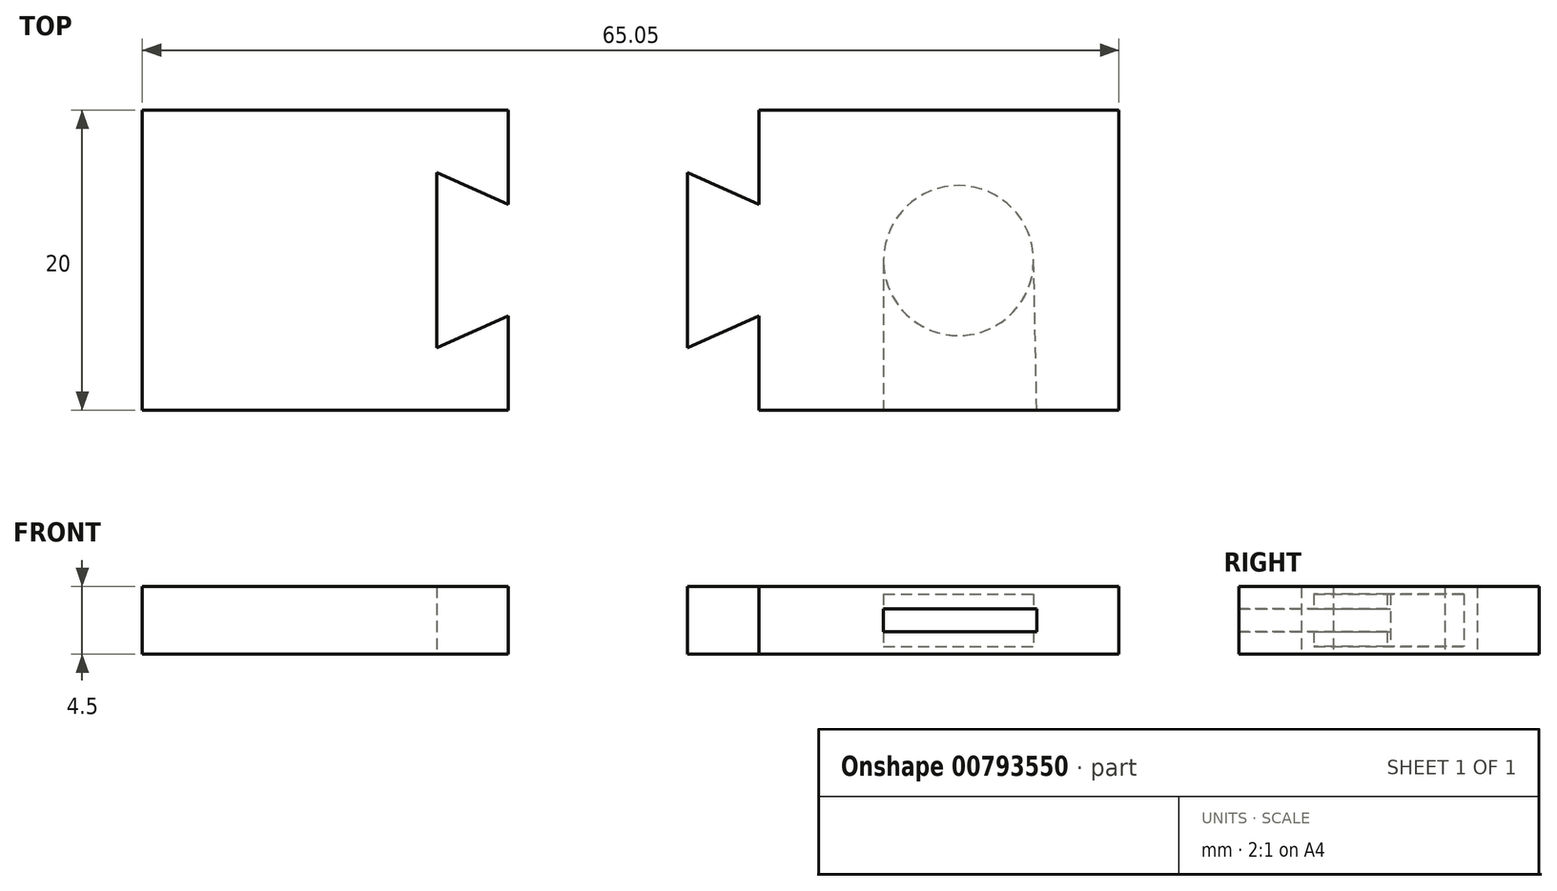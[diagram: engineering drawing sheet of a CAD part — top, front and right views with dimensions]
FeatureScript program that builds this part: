
annotation { "Feature Type Name" : "Feature", "Feature Type Description" : "" }
export const myFeature = defineFeature(function(context is Context, id is Id, definition is map)
    precondition{}
    {
        {
            var Q0;
            Q0=qCreatedBy(makeId("Top.planeOp"),FACE);
            var sketch = newSketch(context, id + "F0", { "sketchPlane" : qUnion([Q0])});
            skLineSegment(sketch, "E0.bottom", {"start": v(-24.37, 20) * mm, "end": v(23.98, 20) * mm});
            skLineSegment(sketch, "E0.top", {"start": v(-24.37, 0) * mm, "end": v(23.98, 0) * mm});
            skLineSegment(sketch, "E0.left", {"start": v(-24.37, 20) * mm, "end": v(-24.37, 0) * mm});
            skLineSegment(sketch, "E0.right", {"start": v(23.98, 20) * mm, "end": v(23.98, 0) * mm});
            skLineSegment(sketch, "E1", {"start": v(0, 20) * mm, "end": v(0, 13.72) * mm});
            skLineSegment(sketch, "E2", {"start": v(0, 13.72) * mm, "end": v(-4.78, 15.86) * mm});
            skLineSegment(sketch, "E3", {"start": v(-4.78, 15.86) * mm, "end": v(-4.78, 4.14) * mm});
            skLineSegment(sketch, "E4", {"start": v(-4.78, 4.14) * mm, "end": v(0, 6.28) * mm});
            skLineSegment(sketch, "E5", {"start": v(0, 6.28) * mm, "end": v(0, 0) * mm});
            skSolve(sketch);
        }
        {
            var Q0;
            {var subQ1=sQuery(id+"F0.wireOp",EDGE,"E0.left");Q0=makeQuery(id+"F0.imprint","IMPRINT",FACE,{"disambiguationData":[TD([[makeQuery(id+"F0.imprint","IMPRINT",EDGE,{"derivedFrom":subQ1}),1.0]])]});}
            extrude(context, id + "F1", {"entities" : qUnion([Q0]), "depth" : 4.5 * mm, "offsetDistance" : 25 * mm});
        }
        {
            var Q0;
            Q0=makeQuery(id+"F1.opExtrude","SWEPT_BODY",BODY,{"disambiguationData":[OSD([sQuery(id+"F0.wireOp",EDGE,"E0.bottom"),sQuery(id+"F0.wireOp",EDGE,"E0.top"),sQuery(id+"F0.wireOp",EDGE,"E0.left"),sQuery(id+"F0.wireOp",EDGE,"E1"),sQuery(id+"F0.wireOp",EDGE,"E2"),sQuery(id+"F0.wireOp",EDGE,"E3"),sQuery(id+"F0.wireOp",EDGE,"E4"),sQuery(id+"F0.wireOp",EDGE,"E5")])]});
            transform(context, id + "F2", {"entities" : qUnion([Q0]), "transformType" : TransformType.TRANSLATION_3D, "dx" : -16.7 * mm, "dy" : 0 * mm, "dz" : 0 * mm, "makeCopy" : false});
        }
        {
            var Q0;
            {var subQ0=sQuery(id+"F0.wireOp",EDGE,"E0.right");Q0=makeQuery(id+"F0.imprint","IMPRINT",FACE,{"disambiguationData":[TD([[makeQuery(id+"F0.imprint","IMPRINT",EDGE,{"derivedFrom":subQ0}),-1.0]])]});}
            extrude(context, id + "F3", {"entities" : qUnion([Q0]), "depth" : 4.5 * mm, "offsetDistance" : 25 * mm});
        }
        {
            var Q0;
            {var subQ1=sQuery(id+"F0.wireOp",EDGE,"E0.left");Q0=makeQuery(id+"F0.imprint","IMPRINT",FACE,{"disambiguationData":[TD([[makeQuery(id+"F0.imprint","IMPRINT",EDGE,{"derivedFrom":subQ1}),1.0]])]});}
            var sketch = newSketch(context, id + "F4", { "sketchPlane" : qUnion([Q0])});
            skCircle(sketch, "E6", {"center": v(13.3, 9.98) * mm, "radius": 5 * mm});
            skLineSegment(sketch, "E7", {"start": v(13.3, 19.95) * mm, "end": v(13.3, 0) * mm, "construction": true});
            skLineSegment(sketch, "E8", {"start": v(8.3, 10.08) * mm, "end": v(8.3, 0) * mm});
            skLineSegment(sketch, "E9", {"start": v(8.3, 0) * mm, "end": v(18.5, 0) * mm});
            skLineSegment(sketch, "E10", {"start": v(18.5, 0) * mm, "end": v(18.3, 10.08) * mm});
            skSolve(sketch);
        }
        {
            var Q0;
            {var subQ0=sQuery(id+"F4.wireOp",EDGE,"E8");var subQ1=sQuery(id+"F4.wireOp",EDGE,"E6");var subQ2=makeQuery(id+"F4.imprint","INTERSECT",VERTEX,{"disambiguationData":[OD(0.0)],"derivedFrom":[subQ1,subQ0]});Q0=makeQuery(id+"F4.imprint","IMPRINT",FACE,{"disambiguationData":[TD([[makeQuery(id+"F4.imprint","IMPRINT",EDGE,{"disambiguationData":[TD([[subQ2,1.0]])],"derivedFrom":subQ1}),1.0]])]});}
            extrude(context, id + "F5", {"entities" : qUnion([Q0]), "operationType" : NewBodyOperationType.REMOVE, "depth" : 4 * mm, "offsetDistance" : 25 * mm, "hasSecondDirection" : true, "secondDirectionOppositeDirection" : true, "secondDirectionDepth" : -0.5 * mm});
        }
        {
            var Q0;
            {var subQ4=sQuery(id+"F4.wireOp",EDGE,"E9");Q0=makeQuery(id+"F4.imprint","IMPRINT",FACE,{"disambiguationData":[TD([[makeQuery(id+"F4.imprint","IMPRINT",EDGE,{"derivedFrom":subQ4}),1.0]])]});}
            extrude(context, id + "F6", {"entities" : qUnion([Q0]), "operationType" : NewBodyOperationType.REMOVE, "depth" : 3 * mm, "offsetDistance" : 25 * mm, "hasSecondDirection" : true, "secondDirectionOppositeDirection" : true, "secondDirectionDepth" : -1.5 * mm});
        }
    });
